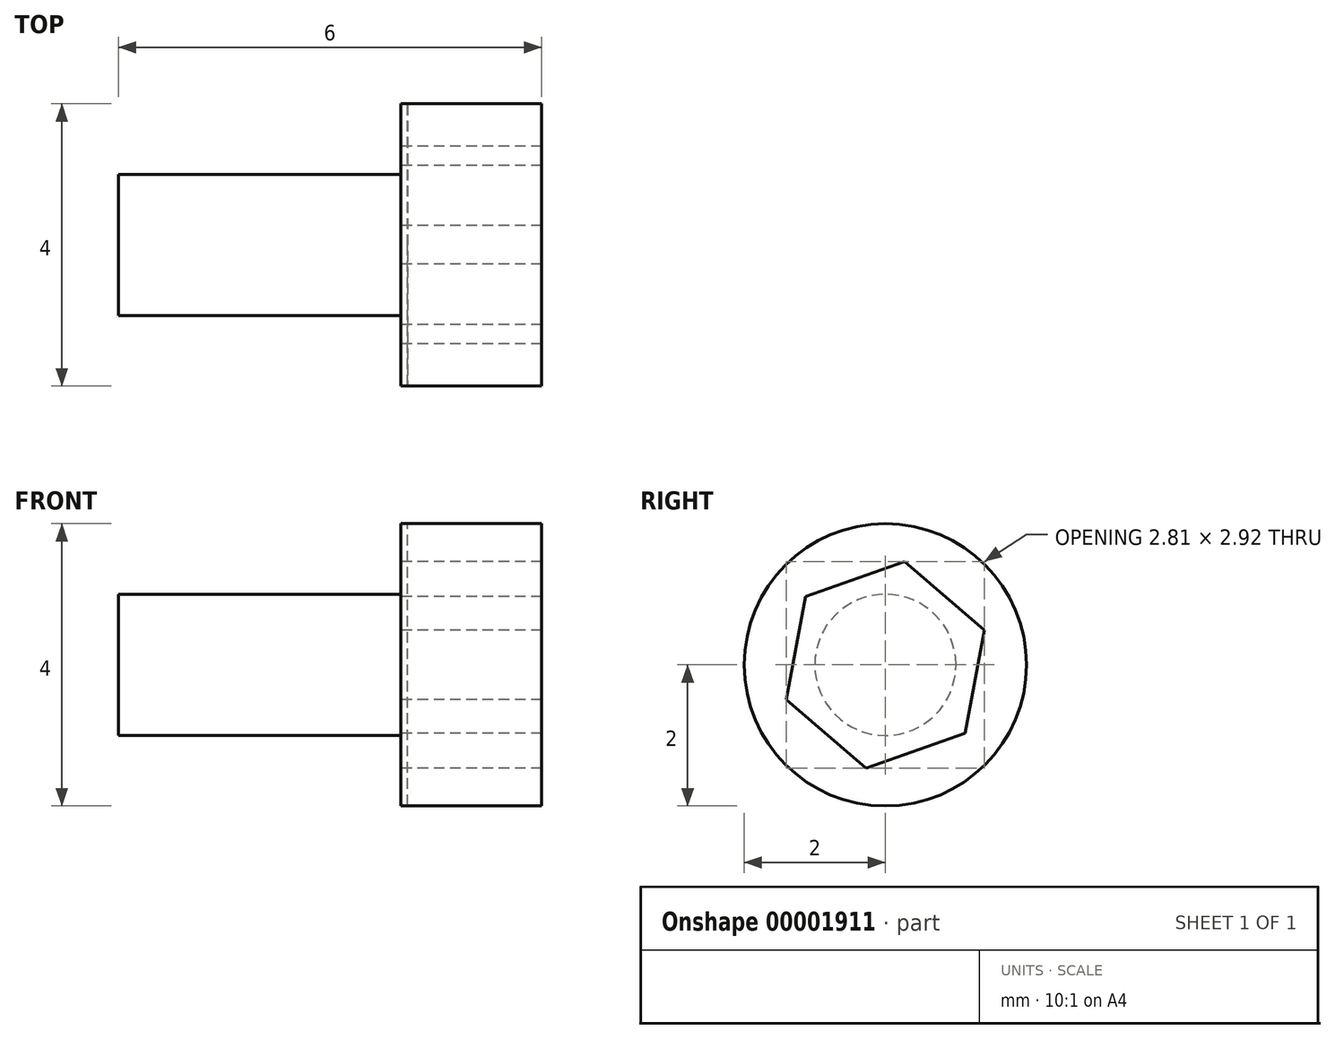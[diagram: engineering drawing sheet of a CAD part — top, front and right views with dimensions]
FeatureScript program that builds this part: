
annotation { "Feature Type Name" : "Feature", "Feature Type Description" : "" }
export const myFeature = defineFeature(function(context is Context, id is Id, definition is map)
    precondition{}
    {
        {
            var Q0;
            Q0=qCreatedBy(makeId("Right.planeOp"),FACE);
            var sketch = newSketch(context, id + "F0", { "sketchPlane" : qUnion([Q0])});
            skCircle(sketch, "E0", {"center": v(0, 0) * mm, "radius": 1 * mm});
            skSolve(sketch);
        }
        {
            var Q0;
            Q0=qCreatedBy(makeId("Right.planeOp"),FACE);
            var sketch = newSketch(context, id + "F1", { "sketchPlane" : qUnion([Q0])});
            skCircle(sketch, "E1", {"center": v(0, 0) * mm, "radius": 2 * mm});
            skLineSegment(sketch, "E2.0", {"start": v(1.13, -0.97) * mm, "end": v(-0.27, -1.46) * mm});
            skLineSegment(sketch, "E2.1", {"start": v(-0.27, -1.46) * mm, "end": v(-1.4, -0.5) * mm});
            skLineSegment(sketch, "E2.2", {"start": v(-1.4, -0.5) * mm, "end": v(-1.13, 0.97) * mm});
            skLineSegment(sketch, "E2.3", {"start": v(-1.13, 0.97) * mm, "end": v(0.27, 1.46) * mm});
            skLineSegment(sketch, "E2.4", {"start": v(0.27, 1.46) * mm, "end": v(1.4, 0.5) * mm});
            skLineSegment(sketch, "E2.5", {"start": v(1.4, 0.5) * mm, "end": v(1.13, -0.97) * mm});
            skSolve(sketch);
        }
        {
            var Q0;
            Q0=makeQuery(id+"F0.imprint","IMPRINT",FACE,{"disambiguationData":[TD([[makeQuery(id+"F0.imprint","IMPRINT",EDGE,{"derivedFrom":sQuery(id+"F0.wireOp",EDGE,"E0")}),1.0]])]});
            extrude(context, id + "F2", {"entities" : qUnion([Q0]), "oppositeDirection" : true, "depth" : 4 * mm});
        }
        {
            var Q0;
            Q0=makeQuery(id+"F1.imprint","IMPRINT",FACE,{"disambiguationData":[TD([[makeQuery(id+"F1.imprint","IMPRINT",EDGE,{"derivedFrom":sQuery(id+"F1.wireOp",EDGE,"E1")}),1.0]])]});
            extrude(context, id + "F3", {"entities" : qUnion([Q0]), "depth" : 2 * mm});
        }
        {
            var Q0;
            Q0=qCreatedBy(makeId("Right.planeOp"),FACE);
            var sketch = newSketch(context, id + "F4", { "sketchPlane" : qUnion([Q0])});
            skCircle(sketch, "E3", {"center": v(0, 0) * mm, "radius": 1.99 * mm});
            skSolve(sketch);
        }
        {
            var Q0;
            Q0=makeQuery(id+"F4.imprint","IMPRINT",FACE,{"disambiguationData":[TD([[makeQuery(id+"F4.imprint","IMPRINT",EDGE,{"derivedFrom":sQuery(id+"F4.wireOp",EDGE,"E3")}),1.0]])]});
            extrude(context, id + "F5", {"entities" : qUnion([Q0]), "depth" : .1 * mm});
        }
    });
